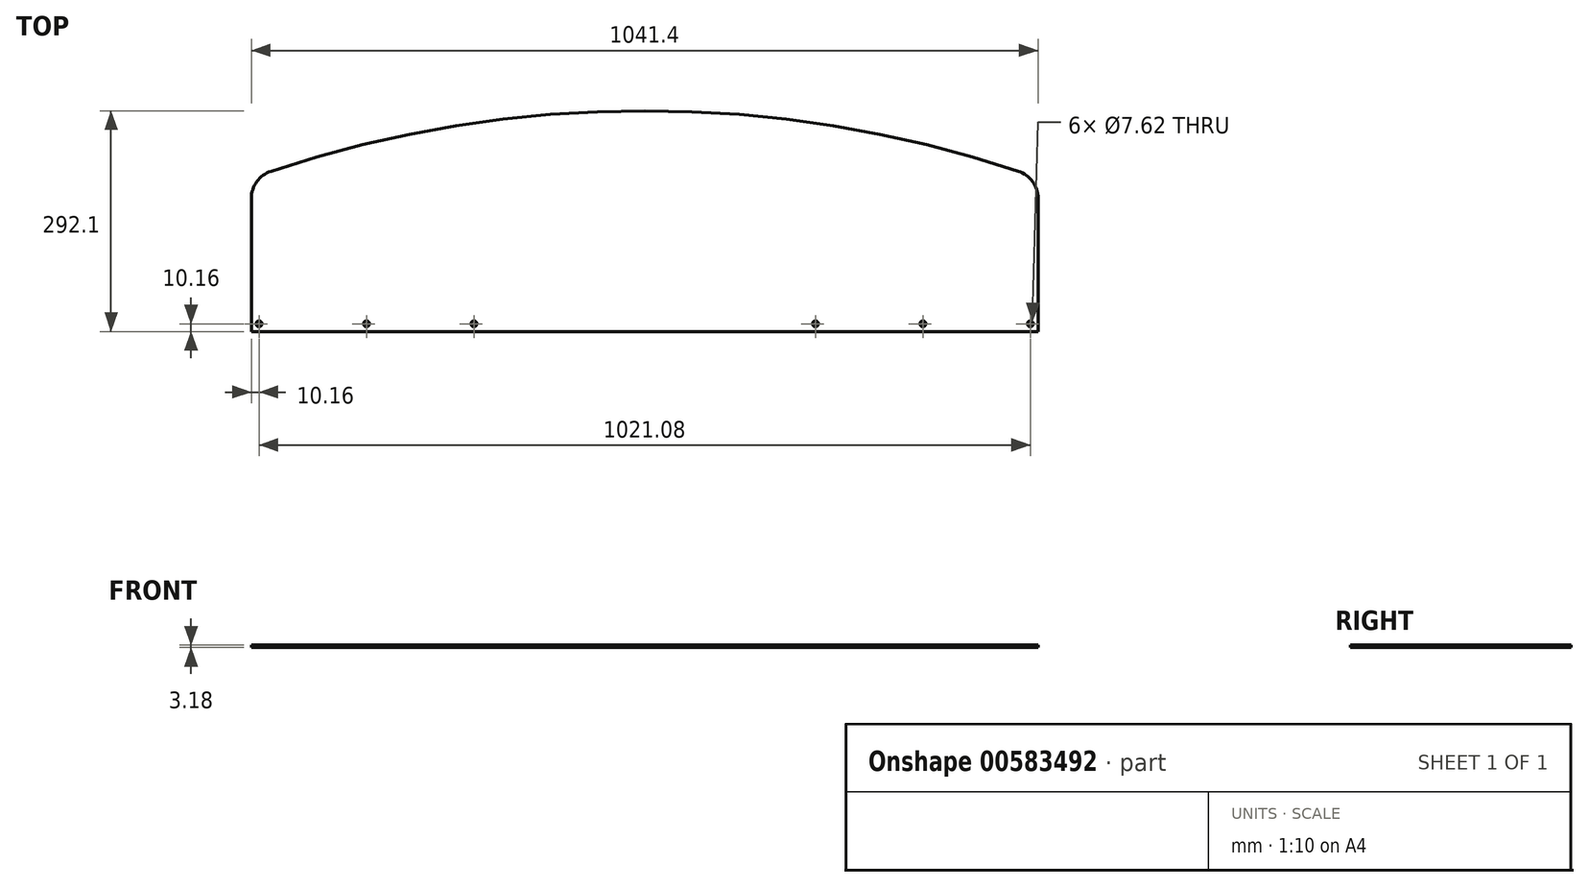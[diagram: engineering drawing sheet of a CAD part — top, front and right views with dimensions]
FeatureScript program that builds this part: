
annotation { "Feature Type Name" : "Feature", "Feature Type Description" : "" }
export const myFeature = defineFeature(function(context is Context, id is Id, definition is map)
    precondition{}
    {
        {
            var Q0;
            Q0=qCreatedBy(makeId("Top.planeOp"),FACE);
            var sketch = newSketch(context, id + "F0", { "sketchPlane" : qUnion([Q0])});
            skLineSegment(sketch, "E0", {"start": v(0, 0) * mm, "end": v(-515.62, 0) * mm});
            skLineSegment(sketch, "E1", {"start": v(0, 0) * mm, "end": v(0, 292.1) * mm, "construction": true});
            skLineSegment(sketch, "E2", {"start": v(0, 0) * mm, "end": v(515.62, 0) * mm});
            skLineSegment(sketch, "E3", {"start": v(520.7, 5.08) * mm, "end": v(520.7, 175.96) * mm});
            skLineSegment(sketch, "E4", {"start": v(-520.7, 5.08) * mm, "end": v(-520.7, 175.96) * mm});
            skArc(sketch, "E5", {"start": v(494.6, 212.12) * mm, "mid": v(0, 292.1) * mm, "end": v(-494.6, 212.12) * mm});
            skPoint(sketch, "E6.visualSharp", {"position": v(-520.7, 203.2) * mm});
            skArc(sketch, "E6.filletArc", {"start": v(-494.6, 212.12) * mm, "mid": v(-513.5, 198.26) * mm, "end": v(-520.7, 175.96) * mm});
            skPoint(sketch, "E7.visualSharp", {"position": v(520.7, 203.2) * mm});
            skArc(sketch, "E7.filletArc", {"start": v(520.7, 175.96) * mm, "mid": v(513.5, 198.26) * mm, "end": v(494.6, 212.12) * mm});
            skPoint(sketch, "E8.visualSharp", {"position": v(-520.7, 0) * mm});
            skPoint(sketch, "E9.visualSharp", {"position": v(520.7, 0) * mm});
            skLineSegment(sketch, "E10", {"start": v(-515.62, 0) * mm, "end": v(-520.7, 0) * mm});
            skLineSegment(sketch, "E11", {"start": v(-520.7, 5.08) * mm, "end": v(-520.7, 0) * mm});
            skLineSegment(sketch, "E12", {"start": v(520.7, 5.08) * mm, "end": v(520.7, 0) * mm});
            skLineSegment(sketch, "E13", {"start": v(520.7, 0) * mm, "end": v(515.62, 0) * mm});
            skSolve(sketch);
        }
        {
            var Q0;
            Q0=makeQuery(id+"F0.imprint","IMPRINT",FACE,{"disambiguationData":[TD([[makeQuery(id+"F0.imprint","IMPRINT",EDGE,{"derivedFrom":sQuery(id+"F0.wireOp",EDGE,"E0")}),-1.0]])]});
            extrude(context, id + "F1", {"entities" : qUnion([Q0]), "depth" : 3.17 * mm, "offsetDistance" : 25.4 * mm});
        }
        {
            var Q0;
            Q0=makeQuery(id+"F1.opExtrude","CAP_FACE",FACE,{"disambiguationData":[OSD([sQuery(id+"F0.wireOp",EDGE,"E0"),sQuery(id+"F0.wireOp",EDGE,"E2"),sQuery(id+"F0.wireOp",EDGE,"E3"),sQuery(id+"F0.wireOp",EDGE,"E4"),sQuery(id+"F0.wireOp",EDGE,"E5"),sQuery(id+"F0.wireOp",EDGE,"E6.filletArc"),sQuery(id+"F0.wireOp",EDGE,"E7.filletArc"),sQuery(id+"F0.wireOp",EDGE,"E10"),sQuery(id+"F0.wireOp",EDGE,"E11"),sQuery(id+"F0.wireOp",EDGE,"E12"),sQuery(id+"F0.wireOp",EDGE,"E13")])],"isStart":false});
            var sketch = newSketch(context, id + "F2", { "sketchPlane" : qUnion([Q0])});
            skCircle(sketch, "E14", {"center": v(-510.54, 10.16) * mm, "radius": 3.81 * mm});
            skCircle(sketch, "E15", {"center": v(-368.3, 10.16) * mm, "radius": 3.81 * mm});
            skCircle(sketch, "E16", {"center": v(-226.06, 10.16) * mm, "radius": 3.81 * mm});
            skLineSegment(sketch, "E17", {"start": v(-368.3, 10.16) * mm, "end": v(589.37, 10.16) * mm, "construction": true});
            skCircle(sketch, "E18", {"center": v(510.54, 10.16) * mm, "radius": 3.81 * mm});
            skCircle(sketch, "E19", {"center": v(368.3, 10.16) * mm, "radius": 3.81 * mm});
            skCircle(sketch, "E20", {"center": v(226.06, 10.16) * mm, "radius": 3.81 * mm});
            skSolve(sketch);
        }
        {
            var Q0;
            Q0=makeQuery(id+"F2.imprint","IMPRINT",FACE,{"disambiguationData":[TD([[makeQuery(id+"F2.imprint","IMPRINT",EDGE,{"derivedFrom":sQuery(id+"F2.wireOp",EDGE,"E18")}),1.0]])]});
            var Q1;
            Q1=makeQuery(id+"F2.imprint","IMPRINT",FACE,{"disambiguationData":[TD([[makeQuery(id+"F2.imprint","IMPRINT",EDGE,{"derivedFrom":sQuery(id+"F2.wireOp",EDGE,"E19")}),1.0]])]});
            var Q2;
            Q2=makeQuery(id+"F2.imprint","IMPRINT",FACE,{"disambiguationData":[TD([[makeQuery(id+"F2.imprint","IMPRINT",EDGE,{"derivedFrom":sQuery(id+"F2.wireOp",EDGE,"E20")}),1.0]])]});
            var Q3;
            Q3=makeQuery(id+"F2.imprint","IMPRINT",FACE,{"disambiguationData":[TD([[makeQuery(id+"F2.imprint","IMPRINT",EDGE,{"derivedFrom":sQuery(id+"F2.wireOp",EDGE,"E16")}),1.0]])]});
            var Q4;
            Q4=makeQuery(id+"F2.imprint","IMPRINT",FACE,{"disambiguationData":[TD([[makeQuery(id+"F2.imprint","IMPRINT",EDGE,{"derivedFrom":sQuery(id+"F2.wireOp",EDGE,"E15")}),1.0]])]});
            var Q5;
            Q5=makeQuery(id+"F2.imprint","IMPRINT",FACE,{"disambiguationData":[TD([[makeQuery(id+"F2.imprint","IMPRINT",EDGE,{"derivedFrom":sQuery(id+"F2.wireOp",EDGE,"E14")}),1.0]])]});
            extrude(context, id + "F3", {"entities" : qUnion([Q0, Q1, Q2, Q3, Q4, Q5]), "operationType" : NewBodyOperationType.REMOVE, "oppositeDirection" : true, "depth" : 25.4 * mm, "offsetDistance" : 25.4 * mm});
        }
    });
